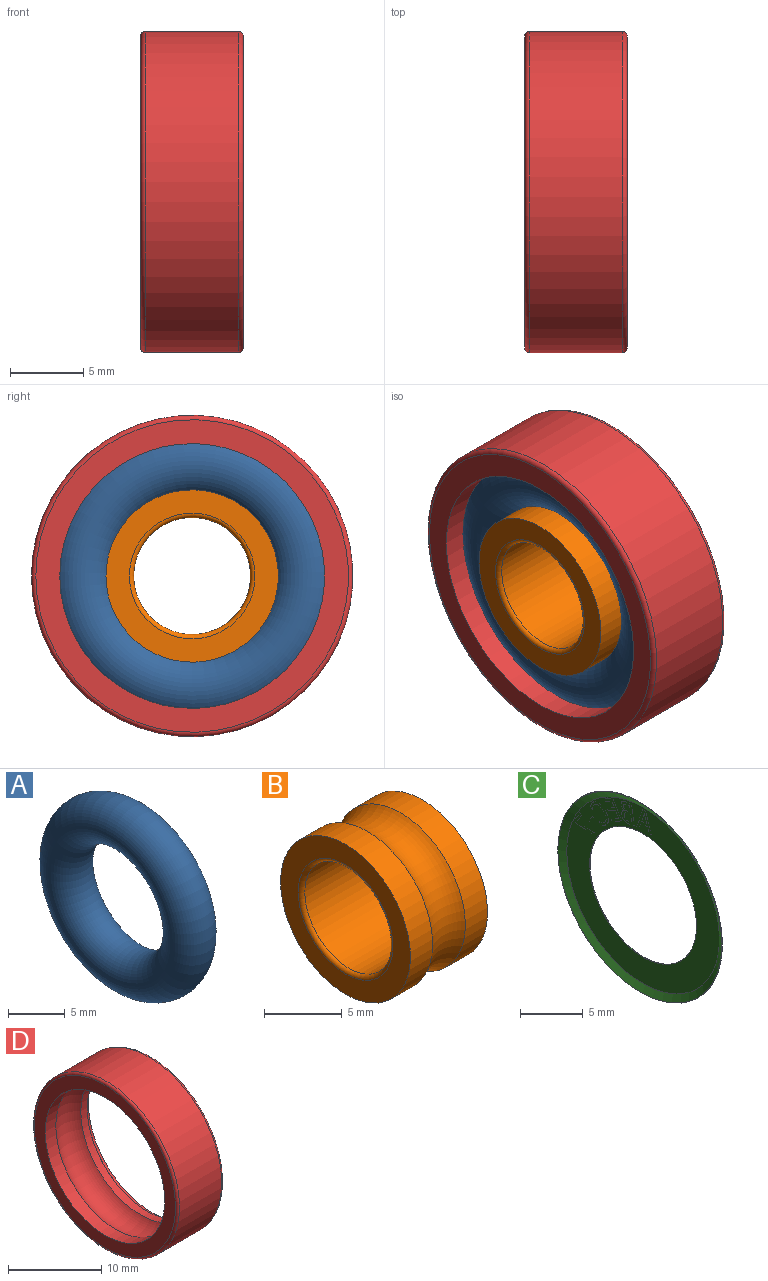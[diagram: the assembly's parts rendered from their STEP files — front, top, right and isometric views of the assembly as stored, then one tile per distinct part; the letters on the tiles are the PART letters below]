
ASSEMBLY  parts=4 mates=3
PART A: 1 faces, bbox 4.7x21.7x21.7 mm
  f0: torus R=7.7mm, axis (1,0,0), area 709.3mm2
PART B: 8 faces, bbox 7x13.1x13.1 mm
  f0: cylinder r=5.9mm len=11.8mm, axis (1,0,0), area 74.7mm2, adj f1,f7
  f1: torus R=7.7mm, axis (1,0,0), area 112.2mm2, adj f0,f2
  f2: cylinder r=5.9mm len=11.8mm, axis (1,0,0), area 74.7mm2, adj f1,f3
  f3: plane 11.8x11.8mm, normal (1,0,0), area 51.3mm2, adj f2,f4
  f4: torus R=4.3mm, axis (1,0,0), area 12.2mm2, adj f3,f5
  f5: cylinder r=4mm len=8mm, axis (1,0,0), area 160.8mm2, adj f4,f6
  f6: torus R=4.3mm, axis (1,0,0), area 12.2mm2, adj f5,f7
  f7: plane 11.8x11.8mm, normal (-1,0,0), area 51.3mm2, adj f0,f6
PART C: 93 faces, bbox 52.6x18.6x18.6 mm
  f0: plane 2.31x1.36mm, normal (1,0,0), area 0.8mm2, adj f1,f2,f3,f4,f5,f6,f7
  f1: plane 0.89x0.52mm, normal (0,0.86,0.51), area 0mm2, adj f0,f2,f5,f84
  f2: plane 0.2x0.12mm, normal (0,0.51,-0.86), area 0mm2, adj f0,f1,f3,f84
  f3: plane 1.09x0.64mm, normal (0,-0.86,-0.51), area 0mm2, adj f0,f2,f4,f84
  f4: plane 0.26x0.15mm, normal (0,-0.51,0.86), area 0mm2, adj f0,f3,f7,f84
  f5: plane 1.99x0.11mm, normal (0,0.05,-1), area 0mm2, adj f0,f1,f6,f84
  f6: plane 0.25x0.14mm, normal (0,0.86,0.51), area 0mm2, adj f0,f5,f7,f84
  f7: plane 1.9x0.11mm, normal (0,-0.06,1), area 0mm2, adj f0,f4,f6,f84
  f8: plane 2x0.67mm, normal (0,0.95,-0.32), area 0mm2, adj f9,f13,f19,f84
  f9: plane 0.33x0.01mm, normal (0,0,-1), area 0mm2, adj f8,f10,f19,f84
  f10: plane 2x0.67mm, normal (0,-0.95,-0.32), area 0mm2, adj f9,f11,f19,f84
  f11: plane 0.28x0.01mm, normal (0,0,1), area 0mm2, adj f10,f16,f19,f84
  f12: plane 0.62x0.01mm, normal (0,0,-1), area 0mm2, adj f17,f18,f19,f86
  f13: plane 0.27x0.01mm, normal (0,0,1), area 0mm2, adj f8,f14,f19,f84
  f14: plane 0.56x0.18mm, normal (0,-0.95,0.31), area 0mm2, adj f13,f15,f19,f84
  f15: plane 0.76x0.01mm, normal (0,0,1), area 0mm2, adj f14,f16,f19,f84
  f16: plane 0.56x0.18mm, normal (0,0.95,0.31), area 0mm2, adj f11,f15,f19,f84
  f17: plane 0.94x0.31mm, normal (0,-0.95,0.31), area 0mm2, adj f12,f18,f19,f86
  f18: plane 0.94x0.31mm, normal (0,0.95,0.31), area 0mm2, adj f12,f17,f19,f86
  f19: plane 2x1.68mm, normal (1,0,0), area 1.2mm2, adj f8,f9,f10,f11,f12,f13,f14,f15
  f20: plane 2.1x1.53mm, normal (1,0,0), area 1.5mm2, adj f21,f22,f23,f24,f25,f26,f27,f28
  f21: extruded ~0.31x0.03mm, area 0mm2, adj f20,f22,f36,f90
  f22: extruded ~0.23x0.16mm, area 0mm2, adj f20,f21,f23,f90
  f23: extruded ~0.22x0.07mm, area 0mm2, adj f20,f22,f24,f90
  f24: extruded ~0.35x0.12mm, area 0mm2, adj f20,f23,f34,f90
  f25: extruded ~0.46x0.04mm, area 0mm2, adj f20,f26,f39,f85
  f26: extruded ~0.26x0.19mm, area 0mm2, adj f20,f25,f27,f85
  f27: extruded ~0.34x0.11mm, area 0mm2, adj f20,f26,f28,f85
  f28: extruded ~0.34x0.11mm, area 0mm2, adj f20,f27,f37,f85
  f29: extruded ~0.5x0.17mm, area 0mm2, adj f20,f30,f40,f84
  f30: extruded ~0.4x0.15mm, area 0mm2, adj f20,f29,f31,f84
  f31: extruded ~0.37x0.35mm, area 0mm2, adj f20,f30,f32,f84
  f32: plane 0.01x0.01mm, normal (0,-0.98,0.18), area 0mm2, adj f20,f31,f33,f84
  f33: extruded ~0.56x0.29mm, area 0mm2, adj f20,f32,f44,f84
  f34: plane 0.25x0.05mm, normal (0,0.18,0.98), area 0mm2, adj f20,f24,f35,f90
  f35: plane 0.58x0.1mm, normal (0,-0.98,0.18), area 0mm2, adj f20,f34,f36,f90
  f36: plane 0.3x0.05mm, normal (0,-0.18,-0.98), area 0mm2, adj f20,f21,f35,f90
  f37: plane 0.3x0.05mm, normal (0,0.18,0.98), area 0mm2, adj f20,f28,f38,f85
  f38: plane 0.73x0.13mm, normal (0,-0.98,0.18), area 0mm2, adj f20,f37,f39,f85
  f39: plane 0.21x0.04mm, normal (0,-0.18,-0.98), area 0mm2, adj f20,f25,f38,f85
  f40: plane 0.52x0.09mm, normal (0,-0.18,-0.98), area 0mm2, adj f20,f29,f41,f84
  f41: plane 1.97x0.36mm, normal (0,0.98,-0.18), area 0mm2, adj f20,f40,f42,f84
  f42: plane 0.56x0.1mm, normal (0,0.18,0.98), area 0mm2, adj f20,f41,f43,f84
  f43: extruded ~0.6x0.08mm, area 0mm2, adj f20,f42,f44,f84
  f44: bspline ~52.59x0.41mm, area 0mm2, adj f20,f33,f43,f84
  f45: plane 1.73x1mm, normal (0,0.87,-0.5), area 0mm2, adj f46,f51,f57,f84
  f46: plane 1.09x0.62mm, normal (0,-0.5,-0.87), area 0mm2, adj f45,f47,f57,f84
  f47: plane 0.21x0.12mm, normal (0,-0.87,0.5), area 0mm2, adj f46,f48,f57,f84
  f48: plane 0.85x0.49mm, normal (0,0.5,0.87), area 0mm2, adj f47,f49,f57,f84
  f49: plane 0.48x0.27mm, normal (0,-0.87,0.5), area 0mm2, adj f48,f50,f57,f84
  f50: plane 0.8x0.46mm, normal (0,-0.5,-0.87), area 0mm2, adj f49,f56,f57,f84
  f51: plane 1.09x0.62mm, normal (0,0.5,0.87), area 0mm2, adj f45,f52,f57,f84
  f52: plane 0.21x0.12mm, normal (0,-0.87,0.5), area 0mm2, adj f51,f53,f57,f84
  f53: plane 0.85x0.49mm, normal (0,-0.5,-0.87), area 0mm2, adj f52,f54,f57,f84
  f54: plane 0.64x0.37mm, normal (0,-0.87,0.5), area 0mm2, adj f53,f55,f57,f84
  f55: plane 0.8x0.46mm, normal (0,0.5,0.87), area 0mm2, adj f54,f56,f57,f84
  f56: plane 0.21x0.12mm, normal (0,-0.87,0.5), area 0mm2, adj f50,f55,f57,f84
  f57: plane 2.36x2.08mm, normal (1,0,0), area 1.2mm2, adj f45,f46,f47,f48,f49,f50,f51,f52
  f58: plane 2.06x2.05mm, normal (1,0,0), area 1mm2, adj f59,f60,f61,f62,f63,f64,f65,f66
  f59: cylinder r=0.57mm len=0.46mm, axis (1,0,0), area 0mm2, adj f58,f60,f69,f84
  f60: extruded ~0.55x0.3mm, area 0mm2, adj f58,f59,f61,f84
  f61: extruded ~0.56x0.3mm, area 0mm2, adj f58,f60,f62,f84
  f62: extruded ~0.45x0.17mm, area 0mm2, adj f58,f61,f63,f84
  f63: extruded ~0.34x0.2mm, area 0mm2, adj f58,f62,f64,f84
  f64: sphere r=1.05mm, area 0mm2, adj f58,f63,f65,f84
  f65: plane 0.01x0.01mm, normal (0,-0.71,-0.71), area 0mm2, adj f58,f64,f66,f84
  f66: plane 0.22x0.22mm, normal (0,-0.71,0.71), area 0mm2, adj f58,f65,f67,f84
  f67: extruded ~0.27x0.11mm, area 0mm2, adj f58,f66,f68,f84
  f68: extruded ~0.29x0.21mm, area 0mm2, adj f58,f67,f78,f84
  f69: extruded ~0.33x0.2mm, area 0mm2, adj f58,f59,f70,f84
  f70: extruded ~0.28x0.04mm, area 0mm2, adj f58,f69,f71,f84
  f71: plane 0.02x0.02mm, normal (0,0.71,0.71), area 0mm2, adj f58,f70,f72,f84
  f72: plane 0.23x0.23mm, normal (0,-0.71,0.71), area 0mm2, adj f58,f71,f73,f84
  f73: bspline ~0.27x0.11mm, area 0mm2, adj f58,f72,f74,f84
  f74: sphere r=1.18mm, area 0mm2, adj f58,f73,f75,f84
  f75: extruded ~0.65x0.27mm, area 0mm2, adj f58,f74,f76,f84
  f76: extruded ~0.72x0.36mm, area 0mm2, adj f58,f75,f77,f84
  f77: extruded ~0.72x0.37mm, area 0mm2, adj f58,f76,f78,f84
  f78: extruded ~0.64x0.27mm, area 0mm2, adj f58,f68,f77,f84
  f79: plane 0.6x0.46mm, normal (0,0.79,0.61), area 0mm2, adj f80,f81,f83,f84
  f80: plane 0.19x0.15mm, normal (0,0.61,-0.79), area 0mm2, adj f79,f82,f83,f84
  f81: plane 0.19x0.15mm, normal (0,-0.61,0.79), area 0mm2, adj f79,f82,f83,f84
  f82: plane 0.6x0.46mm, normal (0,-0.79,-0.61), area 0mm2, adj f80,f81,f83,f84
  f83: plane 0.75x0.65mm, normal (1,0,0), area 0.2mm2, adj f79,f80,f81,f82
  f84: plane 17.29x17.29mm, normal (1,0,0), area 113mm2, adj f1,f2,f3,f4,f5,f6,f7,f8
  f85: plane 0.88x0.8mm, normal (1,0,0), area 0.5mm2, adj f25,f26,f27,f28,f37,f38,f39
  f86: plane 0.94x0.62mm, normal (1,0,0), area 0.3mm2, adj f12,f17,f18
  f87: cone r=8.95mm half-angle=60deg, axis (-1,0,0), area 41.5mm2, adj f88,f92
  f88: plane 17.27x17.27mm, normal (-1,0,0), area 119.4mm2, adj f87,f89
  f89: cylinder r=6.04mm len=12.09mm, axis (-1,0,0), area 1.7mm2, adj f84,f88
  f90: plane 0.78x0.65mm, normal (1,0,0), area 0.4mm2, adj f21,f22,f23,f24,f34,f35,f36
  f91: cone r=8.97mm half-angle=60deg, axis (-1,0,0), area 42.2mm2, adj f84,f92
  f92: cone r=9.28mm half-angle=30deg, axis (1,0,0), area 2.6mm2, adj f87,f91
PART D: 11 faces, bbox 7x23.8x23.8 mm
  f0: plane 21.4x21.4mm, normal (-1,0,0), area 101.7mm2, adj f1,f10
  f1: torus R=10.7mm, axis (1,0,0), area 32.2mm2, adj f0,f2
  f2: cylinder r=11mm len=22mm, axis (1,0,0), area 442.3mm2, adj f1,f3
  f3: torus R=10.7mm, axis (1,0,0), area 32.2mm2, adj f2,f4
  f4: plane 21.4x21.4mm, normal (1,0,0), area 76.2mm2, adj f3,f5
  f5: cylinder r=9.5mm len=19mm, axis (1,0,0), area 19mm2, adj f4,f6
  f6: torus R=9.5mm, axis (1,0,0), area 30.2mm2, adj f5,f7
  f7: plane 19x19mm, normal (1,0,0), area 25.5mm2, adj f6,f8
  f8: cylinder r=9.06mm len=18.13mm, axis (1,0,0), area 55.2mm2, adj f7,f9
  f9: torus R=7.7mm, axis (1,0,0), area 269.4mm2, adj f8,f10
  f10: cylinder r=9.06mm len=18.13mm, axis (1,0,0), area 91.4mm2, adj f0,f9
PLACE A t=(-3.3,0,0)mm
PLACE B t=(-3.3,0,0)mm
PLACE C t=(-3.26,0.17,0.41)mm
PLACE D t=(-3.3,0,0)mm
MATE fastened D.f1 <-> A.f0  axis (1,0,0) through (0.2,0,0)mm
MATE revolute C.f84 <-> B.f0  axis (1,0,0) through (3.7,0,0)mm
MATE revolute D.f1 <-> B.f0  axis (1,0,0) through (3.7,0,0)mm
